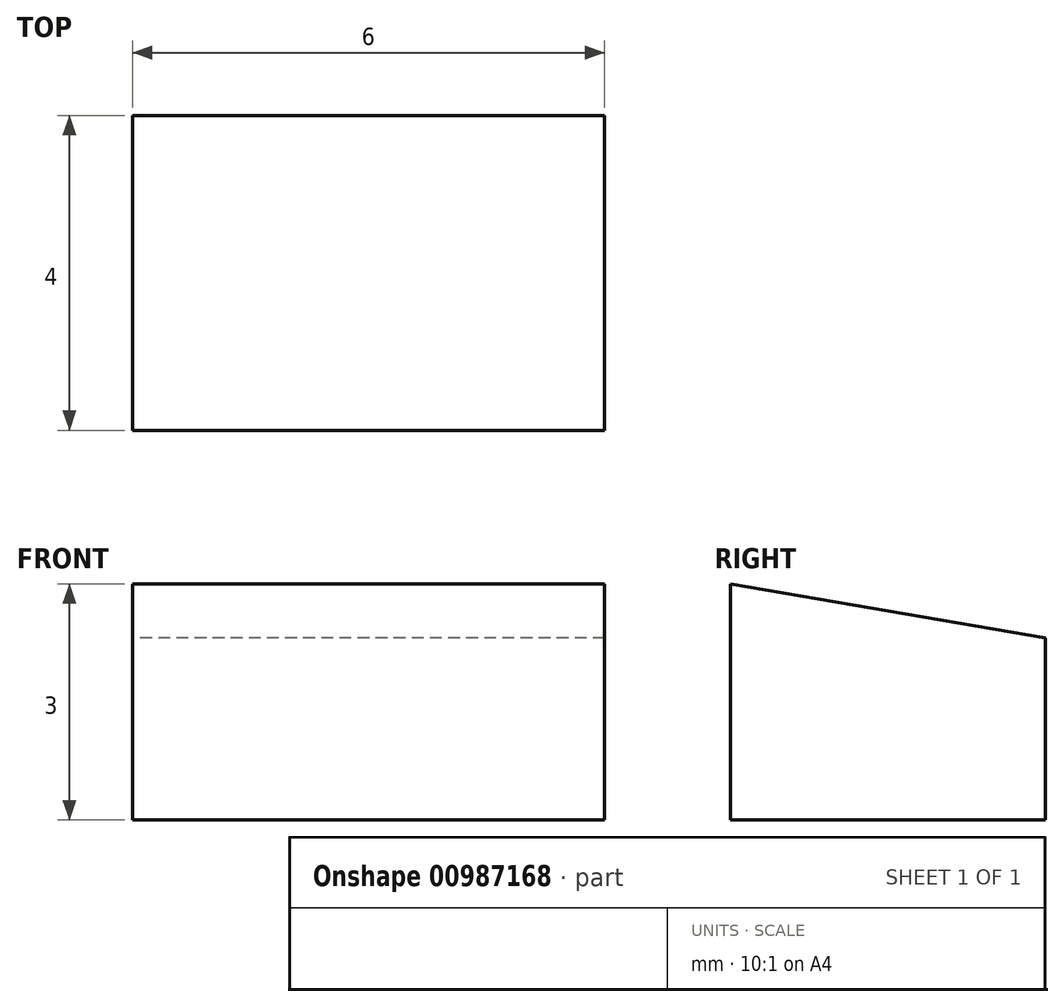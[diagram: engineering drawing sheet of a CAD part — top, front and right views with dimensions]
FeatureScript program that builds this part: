
annotation { "Feature Type Name" : "Feature", "Feature Type Description" : "" }
export const myFeature = defineFeature(function(context is Context, id is Id, definition is map)
    precondition{}
    {
        {
            var Q0;
            Q0=qCreatedBy(makeId("Front.planeOp"),FACE);
            var sketch = newSketch(context, id + "F0", { "sketchPlane" : qUnion([Q0])});
            skLineSegment(sketch, "E0.bottom", {"start": v(0, 0) * mm, "end": v(-6, 0) * mm});
            skLineSegment(sketch, "E0.top", {"start": v(0, 3) * mm, "end": v(-6, 3) * mm});
            skLineSegment(sketch, "E0.left", {"start": v(0, 0) * mm, "end": v(0, 3) * mm});
            skLineSegment(sketch, "E0.right", {"start": v(-6, 0) * mm, "end": v(-6, 3) * mm});
            skSolve(sketch);
        }
        {
            var Q0;
            Q0=makeQuery(id+"F0.imprint","IMPRINT",FACE,{"disambiguationData":[TD([[makeQuery(id+"F0.imprint","IMPRINT",EDGE,{"derivedFrom":sQuery(id+"F0.wireOp",EDGE,"E0.bottom")}),-1.0]])]});
            extrude(context, id + "F1", {"entities" : qUnion([Q0]), "depth" : 4 * mm, "offsetDistance" : 25 * mm});
        }
        {
            var Q0;
            Q0=makeQuery(id+"F1.opExtrude","SWEPT_FACE",FACE,{"disambiguationData":[OSD([sQuery(id+"F0.wireOp",EDGE,"E0.right")])]});
            var sketch = newSketch(context, id + "F2", { "sketchPlane" : qUnion([Q0])});
            skLineSegment(sketch, "E1", {"start": v(4, 3) * mm, "end": v(0, 2.31) * mm});
            skSolve(sketch);
        }
        {
            var Q0;
            Q0 = qSketchRegion(id + "F2", true);
            var Q1;
            {var subQ0=sQuery(id+"F2.wireOp",EDGE,"E1");Q1=makeQuery(id+"F2.imprint","IMPRINT",FACE,{"disambiguationData":[TD([[makeQuery(id+"F2.imprint","IMPRINT",EDGE,{"derivedFrom":subQ0}),-1.0]])]});}
            extrude(context, id + "F3", {"entities" : qUnion([Q0, Q1]), "operationType" : NewBodyOperationType.REMOVE, "oppositeDirection" : true, "depth" : 25 * mm, "offsetDistance" : 25 * mm});
        }
    });
